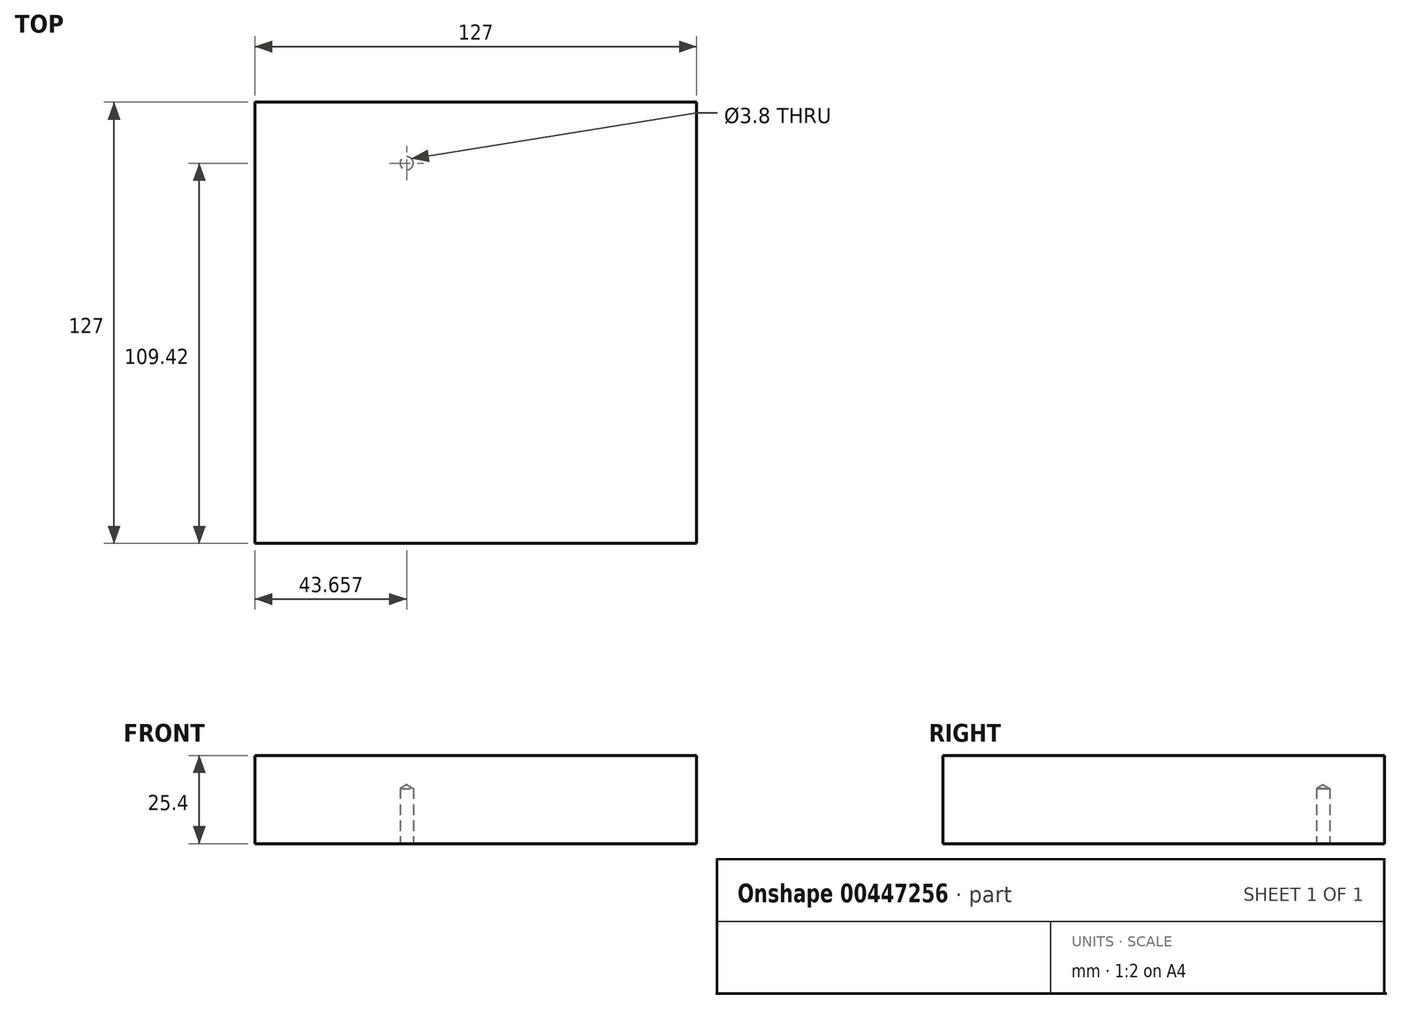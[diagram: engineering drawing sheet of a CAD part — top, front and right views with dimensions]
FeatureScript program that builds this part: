
annotation { "Feature Type Name" : "Feature", "Feature Type Description" : "" }
export const myFeature = defineFeature(function(context is Context, id is Id, definition is map)
    precondition{}
    {
        {
            var Q0;
            Q0=qCreatedBy(makeId("Top.planeOp"),FACE);
            var sketch = newSketch(context, id + "F0", { "sketchPlane" : qUnion([Q0])});
            skLineSegment(sketch, "E0.bottom", {"start": v(63.5, 63.5) * mm, "end": v(-63.5, 63.5) * mm});
            skLineSegment(sketch, "E0.top", {"start": v(63.5, -63.5) * mm, "end": v(-63.5, -63.5) * mm});
            skLineSegment(sketch, "E0.left", {"start": v(63.5, 63.5) * mm, "end": v(63.5, -63.5) * mm});
            skLineSegment(sketch, "E0.right", {"start": v(-63.5, 63.5) * mm, "end": v(-63.5, -63.5) * mm});
            skPoint(sketch, "E0.middle", {"position": v(0, 0) * mm});
            skSolve(sketch);
        }
        {
            var Q0;
            Q0=makeQuery(id+"F0.imprint","IMPRINT",FACE,{"disambiguationData":[TD([[makeQuery(id+"F0.imprint","IMPRINT",EDGE,{"derivedFrom":sQuery(id+"F0.wireOp",EDGE,"E0.bottom")}),1.0]])]});
            var sketch = newSketch(context, id + "F1", { "sketchPlane" : qUnion([Q0])});
            skCircle(sketch, "E1", {"center": v(-19.84, 45.92) * mm, "radius": 4.55 * mm});
            skCircle(sketch, "E2", {"center": v(20.67, 45.16) * mm, "radius": 4.55 * mm});
            skCircle(sketch, "E3", {"center": v(20.67, 14.17) * mm, "radius": 4.55 * mm});
            skCircle(sketch, "E4", {"center": v(-19.84, 14.9) * mm, "radius": 4.55 * mm});
            skSolve(sketch);
        }
        {
            var Q0;
            Q0=makeQuery(id+"F0.imprint","IMPRINT",FACE,{"disambiguationData":[TD([[makeQuery(id+"F0.imprint","IMPRINT",EDGE,{"derivedFrom":sQuery(id+"F0.wireOp",EDGE,"E0.bottom")}),1.0]])]});
            extrude(context, id + "F2", {"entities" : qUnion([Q0]), "depth" : 25.4 * mm, "offsetDistance" : 25.4 * mm});
        }
        {
            var Q0;
            Q0=sQuery(id+"F1.wireOp",VERTEX,"E1.center");
            var Q1;
            Q1=makeQuery(id+"F2.opExtrude","SWEPT_BODY",BODY,{"disambiguationData":[OSD([sQuery(id+"F0.wireOp",EDGE,"E0.bottom"),sQuery(id+"F0.wireOp",EDGE,"E0.top"),sQuery(id+"F0.wireOp",EDGE,"E0.left"),sQuery(id+"F0.wireOp",EDGE,"E0.right")])]});
            hole(context, id + "F3", {"style" : HoleStyle.SIMPLE, "endStyle" : HoleEndStyle.BLIND, "oppositeDirection" : true, "standardTappedOrClearance" : lookupTablePath({ "standard" : "ANSI", "engagement" : "75%", "pitch" : "24 tpi", "size" : "#10", "type" : "Tapped" }), "standardBlindInLast" : lookupTablePath({ "standard" : "ANSI", "engagement" : "75%", "pitch" : "24 tpi", "size" : "#10", "type" : "Tapped" }), "holeDiameter" : 3.8 * mm, "majorDiameter" : 4.83 * mm, "showTappedDepth" : true, "holeDepth" : 15.88 * mm, "isTappedThrough" : true, "tappedDepth" : 12.7 * mm, "tapClearance" : 3, "startFromSketch" : true, "locations" : qUnion([Q0]), "scope" : qUnion([Q1])});
        }
    });
